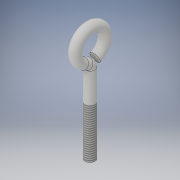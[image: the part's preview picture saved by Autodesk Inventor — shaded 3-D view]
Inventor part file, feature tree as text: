
AUTODESK INVENTOR PART (.ipt)
format: ipt  version: 2018.2 (Build 222227000, 227)  size: 153,088 bytes
history: native  units: in
note: dims shown in document units (in); Inventor stores cm internally (conversion verified against a paired STEP export)
features: sketch x7, plane x4, revolve x3, extrude x2, thread x1
ambient origin geometry x8: Origin, YZ Plane, XZ Plane, XY Plane, X Axis, Y Axis, Z Axis, Center Point
bodies: Solid1 (feature_tree)
feature tree (17):
  extrude  "Extrusion1"  Depth=2.0in TaperAngle=0.0deg
  thread  "Thread1"  [1 undecoded]
  sketch  "Sketch2"  dims[d5=90.0deg d11=2.3363in]
  plane  "Work Plane1"
  sketch  "Sketch8"  dims[d13=0.1929in d17=90.0deg]
  sketch  "Sketch9"  dims[d18=0.1718in d19=0.125in]
  revolve  "Revolution4"  [1 undecoded]
  plane  "Work Plane3"
  sketch  "Sketch12"  dims[d20=0.1718in d21=2.0in d22=0.0in]
  plane  "Work Plane6"
  revolve  "Revolution7"  Angle=90.0deg
  plane  "Work Plane7"
  revolve  "Revolution8"  [1 undecoded]
  extrude  "Extrusion2"  Depth=2.0in TaperAngle=0.0deg
  sketch  "Sketch1"  dims[d0=0.25in d1=2.0in d2=0.0in d3=1.25in d4=0.0in]
  sketch  "Sketch14"
  sketch  "Sketch15"
note: 3 required parameter values undecoded (feature->parameter linkage not recoverable at this tier; creation-order binding heuristic only, values carry confidence <= 0.55)